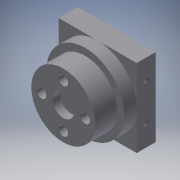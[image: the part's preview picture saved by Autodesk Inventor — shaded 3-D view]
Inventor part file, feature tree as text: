
AUTODESK INVENTOR PART (.ipt)
format: ipt  version: 2018 (Build 220112000, 112)  size: 192,512 bytes
history: native  units: mm
features: sketch x7, extrude x4, hole x3, projected_geometry x3
ambient origin geometry x8: Origin, YZ Plane, XZ Plane, XY Plane, X Axis, Y Axis, Z Axis, Center Point
bodies: Solid1 (feature_tree)
feature tree (17):
  extrude  "Extrusion1"  Depth=7.05mm TaperAngle=0.0deg
  extrude  "Extrusion2"  Depth=4.0mm TaperAngle=0.0deg
  extrude  "Extrusion3"  Depth=25.0mm
  hole  "Hole1"  [1 undecoded]
  extrude  "Extrusion4"  Depth=7.0mm
  hole  "Hole2"  [1 undecoded]
  hole  "Hole3"  [1 undecoded]
  sketch  "Sketch1"  dims[d0=20.5mm d1=7.05mm d2=0.0mm]
  sketch  "Sketch2"  dims[d3=24.95mm d4=4.0mm d5=0.0mm]
  sketch  "Sketch3"  dims[d6=25.0mm d7=25.0mm]
  projected_geometry  "Projected Loop1"
  sketch  "Sketch4"  dims[d8=6.1mm d9=0.0mm d10=12.0mm]
  projected_geometry  "Projected Loop2"
  sketch  "Sketch5"  dims[d11=3.0mm]
  sketch  "Sketch6"  dims[d12=1.567mm d13=25.0mm d14=4.0mm d15=2.0mm d16=90.0deg d17=6.3mm d18=20.594885mm d19=7.0mm]
  sketch  "Sketch7"  dims[d20=2.5mm d21=0.0mm d22=14.0mm d23=3.1mm d24=25.0mm d25=6.3mm d26=2.0mm d27=90.0deg d28=6.3mm d29=20.594885mm d30=5.7mm d31=25.0mm d32=6.3mm d33=2.0mm d34=90.0deg d35=3.2mm d36=17.453293mm]
  projected_geometry  "Projected Loop3"
note: 3 required parameter values undecoded (feature->parameter linkage not recoverable at this tier; creation-order binding heuristic only, values carry confidence <= 0.55)
